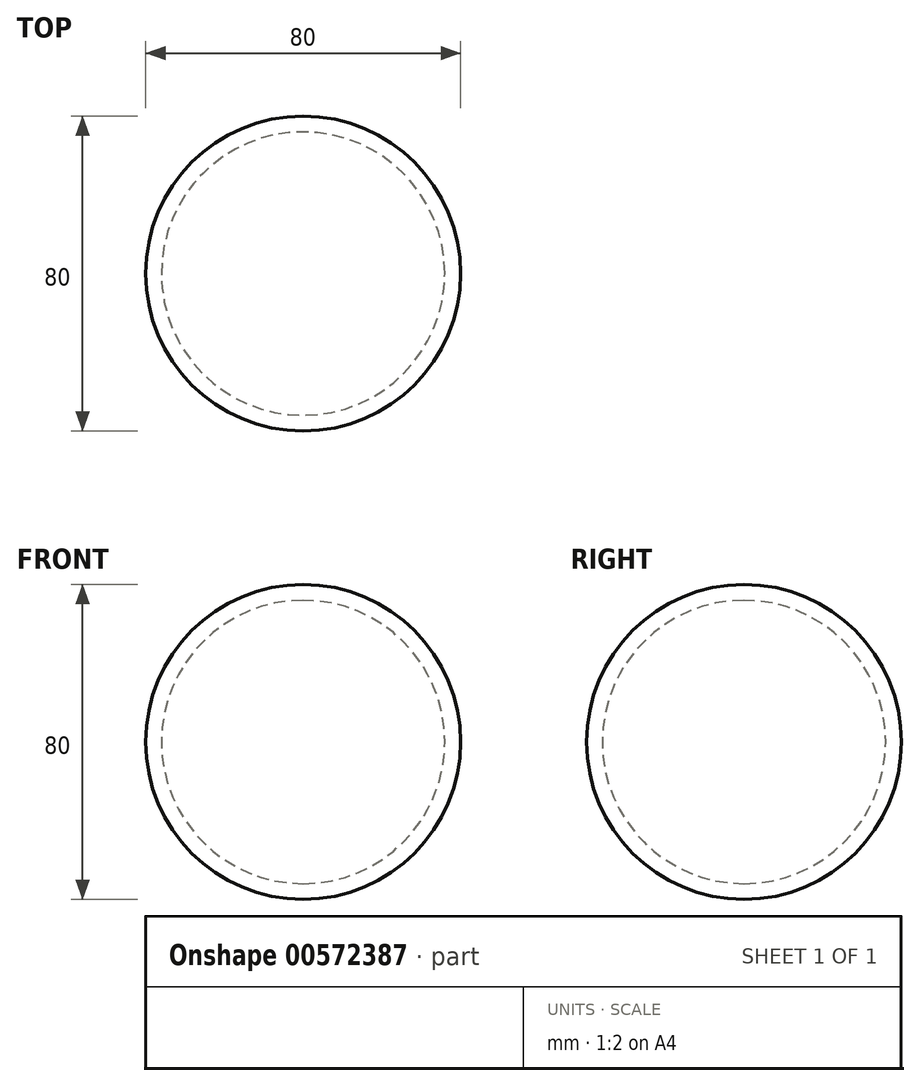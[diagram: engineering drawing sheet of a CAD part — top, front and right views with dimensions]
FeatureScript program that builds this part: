
annotation { "Feature Type Name" : "Feature", "Feature Type Description" : "" }
export const myFeature = defineFeature(function(context is Context, id is Id, definition is map)
    precondition{}
    {
        {
            var Q0;
            Q0=qCreatedBy(makeId("Front.planeOp"),FACE);
            var sketch = newSketch(context, id + "F0", { "sketchPlane" : qUnion([Q0])});
            skArc(sketch, "E0", {"start": v(0, 40) * mm, "mid": v(40, 0) * mm, "end": v(0, -40) * mm});
            skArc(sketch, "E1", {"start": v(0, 36) * mm, "mid": v(36, 0) * mm, "end": v(0, -36) * mm});
            skLineSegment(sketch, "E2", {"start": v(0, 40) * mm, "end": v(0, 36) * mm});
            skLineSegment(sketch, "E3", {"start": v(0, -36) * mm, "end": v(0, -40) * mm});
            skSolve(sketch);
        }
        {
            var Q0;
            Q0=qCreatedBy(makeId("Front.planeOp"),FACE);
            var sketch = newSketch(context, id + "F1", { "sketchPlane" : qUnion([Q0])});
            skLineSegment(sketch, "E4", {"start": v(0, 45) * mm, "end": v(0, -45) * mm});
            skSolve(sketch);
        }
        {
            var Q0;
            Q0 = qSketchRegion(id + "F0", true);
            var Q1;
            Q1=sQuery(id+"F1.wireOp",EDGE,"E4");
            revolve(context, id + "F2", {"entities" : qUnion([Q0]), "axis" : qUnion([Q1]), "revolveType" : RevolveType.FULL});
        }
    });
